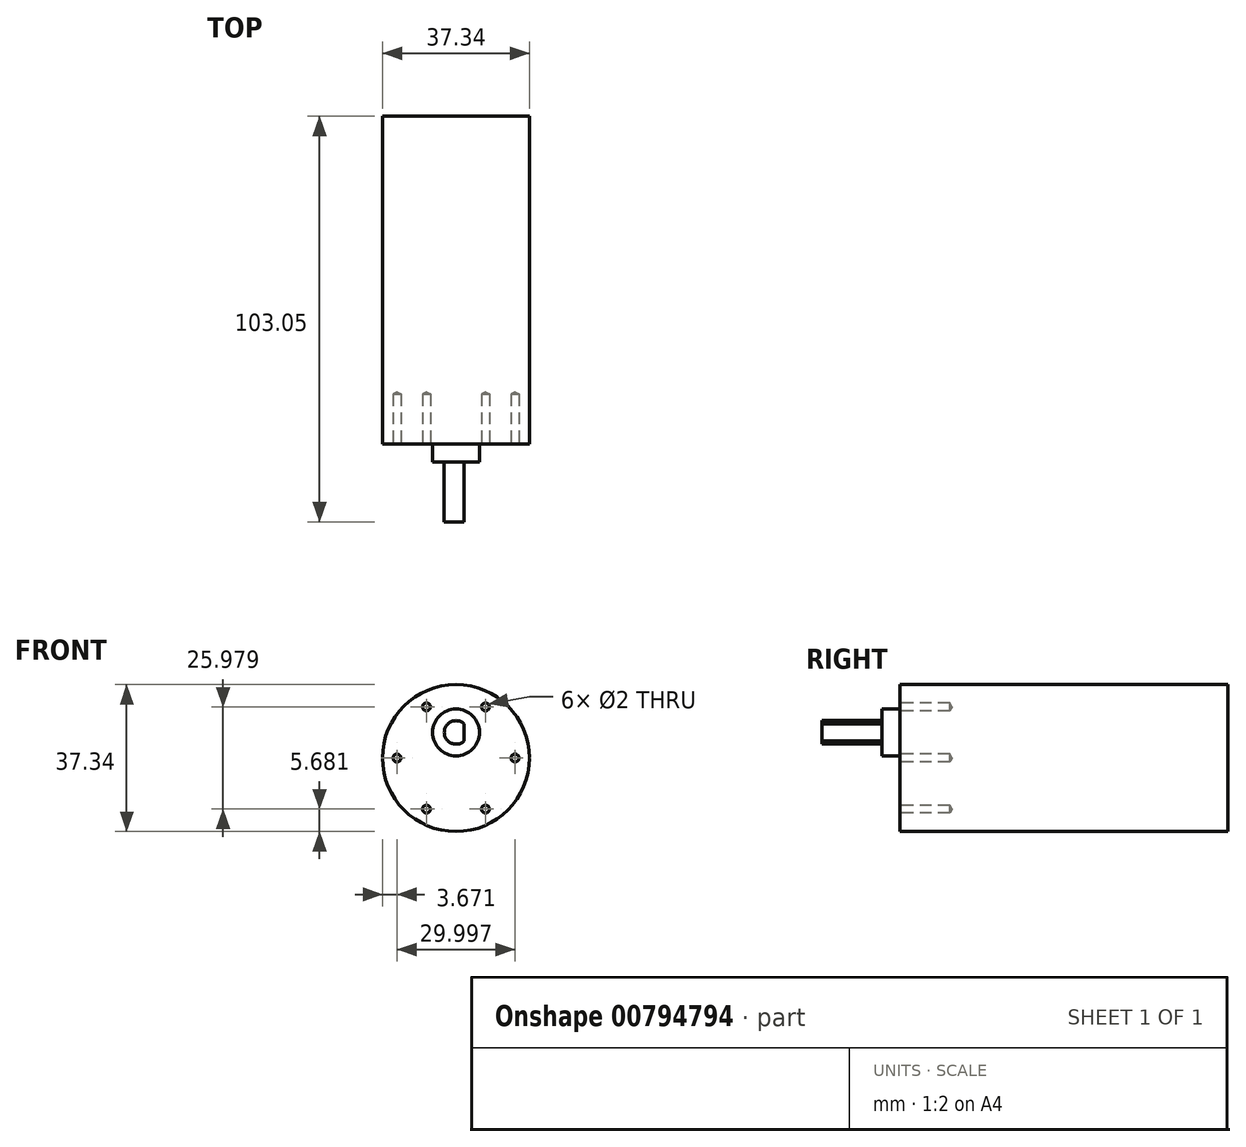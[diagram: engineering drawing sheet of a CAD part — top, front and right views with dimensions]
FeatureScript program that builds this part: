
annotation { "Feature Type Name" : "Feature", "Feature Type Description" : "" }
export const myFeature = defineFeature(function(context is Context, id is Id, definition is map)
    precondition{}
    {
        {
            var Q0;
            Q0=qCreatedBy(makeId("Front.planeOp"),FACE);
            var sketch = newSketch(context, id + "F0", { "sketchPlane" : qUnion([Q0])});
            skCircle(sketch, "E0", {"center": v(0, 0) * mm, "radius": 18.67 * mm});
            skCircle(sketch, "E1", {"center": v(0, 0) * mm, "radius": 15 * mm});
            skPoint(sketch, "E2", {"position": v(15, 0) * mm});
            skPoint(sketch, "E3.1.0", {"position": v(7.5, 12.99) * mm});
            skPoint(sketch, "E3.2.0", {"position": v(-7.5, 12.99) * mm});
            skPoint(sketch, "E3.3.0", {"position": v(-15, 0) * mm});
            skPoint(sketch, "E3.4.0", {"position": v(-7.5, -12.99) * mm});
            skPoint(sketch, "E3.5.0", {"position": v(7.5, -12.99) * mm});
            skPoint(sketch, "E4", {"position": v(0, 6.5) * mm});
            skCircle(sketch, "E5", {"center": v(0, 6.5) * mm, "radius": 5.97 * mm});
            skSolve(sketch);
        }
        {
            var Q0;
            Q0=makeQuery(id+"F0.imprint","IMPRINT",FACE,{"disambiguationData":[TD([[makeQuery(id+"F0.imprint","IMPRINT",EDGE,{"derivedFrom":sQuery(id+"F0.wireOp",EDGE,"E0")}),1.0]])]});
            var Q1;
            Q1=makeQuery(id+"F0.imprint","IMPRINT",FACE,{"disambiguationData":[TD([[makeQuery(id+"F0.imprint","IMPRINT",EDGE,{"derivedFrom":sQuery(id+"F0.wireOp",EDGE,"E1")}),1.0]])]});
            var Q2;
            Q2=makeQuery(id+"F0.imprint","IMPRINT",FACE,{"disambiguationData":[TD([[makeQuery(id+"F0.imprint","IMPRINT",EDGE,{"derivedFrom":sQuery(id+"F0.wireOp",EDGE,"E5")}),1.0]])]});
            extrude(context, id + "F1", {"entities" : qUnion([Q0, Q1, Q2]), "oppositeDirection" : true, "depth" : 83.31 * mm, "offsetDistance" : 25.4 * mm});
        }
        {
            var Q0;
            Q0=sQuery(id+"F0.wireOp",VERTEX,"E3.2.0");
            var Q1;
            Q1=sQuery(id+"F0.wireOp",VERTEX,"E3.1.0");
            var Q2;
            Q2=sQuery(id+"F0.wireOp",VERTEX,"E2");
            var Q3;
            Q3=sQuery(id+"F0.wireOp",VERTEX,"E3.5.0");
            var Q4;
            Q4=sQuery(id+"F0.wireOp",VERTEX,"E3.4.0");
            var Q5;
            Q5=sQuery(id+"F0.wireOp",VERTEX,"E3.3.0");
            var Q6;
            Q6=makeQuery(id+"F1.opExtrude","SWEPT_BODY",BODY,{"disambiguationData":[OSD([sQuery(id+"F0.wireOp",EDGE,"E0")])]});
            hole(context, id + "F2", {"style" : HoleStyle.SIMPLE, "endStyle" : HoleEndStyle.BLIND, "holeDiameter" : 2 * mm, "majorDiameter" : 4 * mm, "holeDepth" : 12.7 * mm, "isTappedThrough" : true, "tappedDepth" : 16.95 * mm, "tapClearance" : 3, "startFromSketch" : true, "locations" : qUnion([Q0, Q1, Q2, Q3, Q4, Q5]), "scope" : qUnion([Q6])});
        }
        {
            var Q0;
            Q0=makeQuery(id+"F0.imprint","IMPRINT",FACE,{"disambiguationData":[TD([[makeQuery(id+"F0.imprint","IMPRINT",EDGE,{"derivedFrom":sQuery(id+"F0.wireOp",EDGE,"E5")}),1.0]])]});
            extrude(context, id + "F3", {"entities" : qUnion([Q0]), "depth" : 4.5 * mm, "offsetDistance" : 25.4 * mm});
        }
        {
            var Q0;
            Q0=makeQuery(id+"F3.opExtrude","CAP_FACE",FACE,{"disambiguationData":[OSD([sQuery(id+"F0.wireOp",EDGE,"E5")])],"isStart":false});
            var sketch = newSketch(context, id + "F4", { "sketchPlane" : qUnion([Q0])});
            skArc(sketch, "E6", {"start": v(2.1, 8.62) * mm, "mid": v(-2.98, 6.5) * mm, "end": v(2.1, 4.38) * mm});
            skLineSegment(sketch, "E7", {"start": v(2.1, 8.62) * mm, "end": v(2.1, 4.38) * mm});
            skSolve(sketch);
        }
        {
            var Q0;
            Q0=makeQuery(id+"F4.imprint","IMPRINT",FACE,{"disambiguationData":[TD([[makeQuery(id+"F4.imprint","IMPRINT",EDGE,{"derivedFrom":sQuery(id+"F4.wireOp",EDGE,"E6")}),1.0]])]});
            extrude(context, id + "F5", {"entities" : qUnion([Q0]), "operationType" : NewBodyOperationType.ADD, "depth" : 15.24 * mm, "offsetDistance" : 25.4 * mm});
        }
    });
